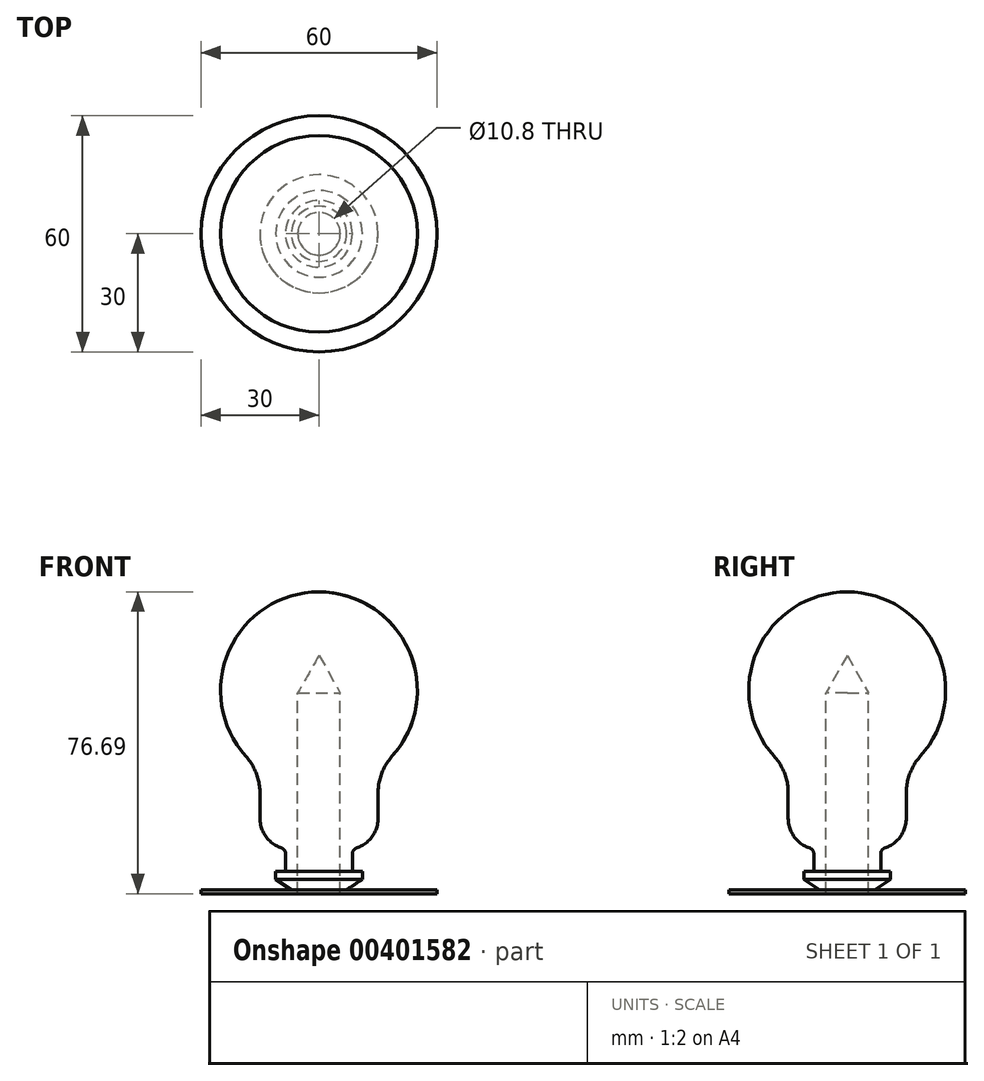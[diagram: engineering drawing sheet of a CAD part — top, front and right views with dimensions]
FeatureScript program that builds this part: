
annotation { "Feature Type Name" : "Feature", "Feature Type Description" : "" }
export const myFeature = defineFeature(function(context is Context, id is Id, definition is map)
    precondition{}
    {
        {
            var Q0;
            Q0=qCreatedBy(makeId("Front.planeOp"),FACE);
            var sketch = newSketch(context, id + "F0", { "sketchPlane" : qUnion([Q0])});
            skArc(sketch, "E0", {"start": v(15, -20) * mm, "mid": v(23.72, 7.9) * mm, "end": v(0, 25) * mm});
            skLineSegment(sketch, "E1", {"start": v(0, 25) * mm, "end": v(0, 8.9) * mm});
            skLineSegment(sketch, "E2", {"start": v(15, -35) * mm, "end": v(15, -20) * mm});
            skPoint(sketch, "E3.visualSharp", {"position": v(15, -40) * mm});
            skLineSegment(sketch, "E4", {"start": v(8.5, -46) * mm, "end": v(11, -46) * mm});
            skLineSegment(sketch, "E5", {"start": v(11, -46) * mm, "end": v(11, -48) * mm});
            skLineSegment(sketch, "E6", {"start": v(7, -50.69) * mm, "end": v(5.4, -50.69) * mm});
            skPoint(sketch, "E7.end.orphan", {"position": v(9.5, -39.77) * mm});
            skLineSegment(sketch, "E8", {"start": v(8.5, -40) * mm, "end": v(8.5, -46) * mm});
            skLineSegment(sketch, "E9", {"start": v(11, -48) * mm, "end": v(7, -50.69) * mm});
            skLineSegment(sketch, "E10", {"start": v(8.5, -40) * mm, "end": v(10, -40) * mm});
            skPoint(sketch, "E11.orphan", {"position": v(8.5, -39.77) * mm});
            skLineSegment(sketch, "E12", {"start": v(5.4, -50.69) * mm, "end": v(5.4, -0.69) * mm});
            skLineSegment(sketch, "E13", {"start": v(5.4, -0.69) * mm, "end": v(0, 8.9) * mm});
            skPoint(sketch, "E14.start.orphan", {"position": v(0, -40) * mm});
            skPoint(sketch, "E15.orphan", {"position": v(0, -50.69) * mm});
            skLineSegment(sketch, "E16", {"start": v(15, -35) * mm, "end": v(15, -40) * mm});
            skLineSegment(sketch, "E17", {"start": v(10, -40) * mm, "end": v(15, -40) * mm});
            skSolve(sketch);
        }
        {
            var Q0;
            Q0=makeQuery(id+"F0.imprint","IMPRINT",FACE,{"disambiguationData":[TD([[makeQuery(id+"F0.imprint","IMPRINT",EDGE,{"derivedFrom":sQuery(id+"F0.wireOp",EDGE,"E0")}),1.0]])]});
            var Q1;
            Q1=sQuery(id+"F0.wireOp",EDGE,"E1");
            revolve(context, id + "F1", {"entities" : qUnion([Q0]), "axis" : qUnion([Q1]), "revolveType" : RevolveType.FULL});
        }
        {
            var Q0;
            Q0=makeQuery(id+"F1.opRevolve","SWEPT_EDGE",EDGE,{"disambiguationData":[OSD([sQuery(id+"F0.wireOp",EDGE,"E8"),sQuery(id+"F0.wireOp",EDGE,"E10")])]});
            fillet(context, id + "F2", {"entities" : qUnion([Q0]), "radius" : 1.5 * mm, "tangentPropagation" : true, "allowEdgeOverflow" : false});
        }
        {
            var Q0;
            Q0=makeQuery(id+"F1.opRevolve","SWEPT_EDGE",EDGE,{"disambiguationData":[OSD([sQuery(id+"F0.wireOp",EDGE,"E0"),sQuery(id+"F0.wireOp",EDGE,"E2")])]});
            fillet(context, id + "F3", {"entities" : qUnion([Q0]), "radius" : 14.1 * mm, "tangentPropagation" : true, "allowEdgeOverflow" : false});
        }
        {
            var Q0;
            Q0=makeQuery(id+"F1.opRevolve","SWEPT_FACE",FACE,{"disambiguationData":[OSD([sQuery(id+"F0.wireOp",EDGE,"E6")])]});
            cPlane(context, id + "F4", {"entities" : qUnion([Q0]), "cplaneType" : CPlaneType.OFFSET, "offset" : 0 * mm, "oppositeDirection" : true, "width" : 150 * mm, "height" : 150 * mm});
        }
        {
            var Q0;
            Q0=qCreatedBy(id+"F4.planeOp",FACE);
            var sketch = newSketch(context, id + "F5", { "sketchPlane" : qUnion([Q0])});
            skCircle(sketch, "E18", {"center": v(0, 0) * mm, "radius": 30 * mm});
            skSolve(sketch);
        }
        {
            var Q0;
            Q0 = qSketchRegion(id + "F5", true);
            extrude(context, id + "F6", {"entities" : qUnion([Q0]), "operationType" : NewBodyOperationType.ADD, "depth" : 1 * mm});
        }
        {
            var Q0;
            Q0=makeQuery(id+"F6.opExtrude","CAP_FACE",FACE,{"disambiguationData":[OSD([sQuery(id+"F5.wireOp",EDGE,"E18")])],"isStart":false});
            var sketch = newSketch(context, id + "F7", { "sketchPlane" : qUnion([Q0])});
            skCircle(sketch, "E19", {"center": v(0, 0) * mm, "radius": 5.4 * mm});
            skSolve(sketch);
        }
        {
            var Q0;
            Q0=sQuery(id+"F7.wireOp",VERTEX,"E19.center");
            var Q1;
            Q1=makeQuery(id+"F1.opRevolve","SWEPT_BODY",BODY,{"disambiguationData":[OSD([sQuery(id+"F0.wireOp",EDGE,"E0"),sQuery(id+"F0.wireOp",EDGE,"E1"),sQuery(id+"F0.wireOp",EDGE,"E2"),sQuery(id+"F0.wireOp",EDGE,"E3.filletArc"),sQuery(id+"F0.wireOp",EDGE,"E4"),sQuery(id+"F0.wireOp",EDGE,"E5"),sQuery(id+"F0.wireOp",EDGE,"E6"),sQuery(id+"F0.wireOp",EDGE,"E8"),sQuery(id+"F0.wireOp",EDGE,"E9"),sQuery(id+"F0.wireOp",EDGE,"E10"),sQuery(id+"F0.wireOp",EDGE,"E12"),sQuery(id+"F0.wireOp",EDGE,"E13")])]});
            hole(context, id + "F8", {"style" : HoleStyle.C_BORE, "endStyle" : HoleEndStyle.BLIND, "holeDiameter" : 10.8 * mm, "cBoreDiameter" : 10.8 * mm, "cBoreDepth" : 10.8 * mm, "holeDepth" : 50 * mm, "isTappedThrough" : true, "tappedDepth" : 12 * mm, "tapClearance" : 3, "startFromSketch" : true, "locations" : qUnion([Q0]), "scope" : qUnion([Q1])});
        }
        {
            var Q0;
            Q0=makeQuery(id+"F1.opRevolve","SWEPT_EDGE",EDGE,{"disambiguationData":[OSD([sQuery(id+"F0.wireOp",EDGE,"E16"),sQuery(id+"F0.wireOp",EDGE,"E17")])]});
            fillet(context, id + "F9", {"entities" : qUnion([Q0]), "radius" : 8 * mm, "tangentPropagation" : true, "allowEdgeOverflow" : false});
        }
    });
